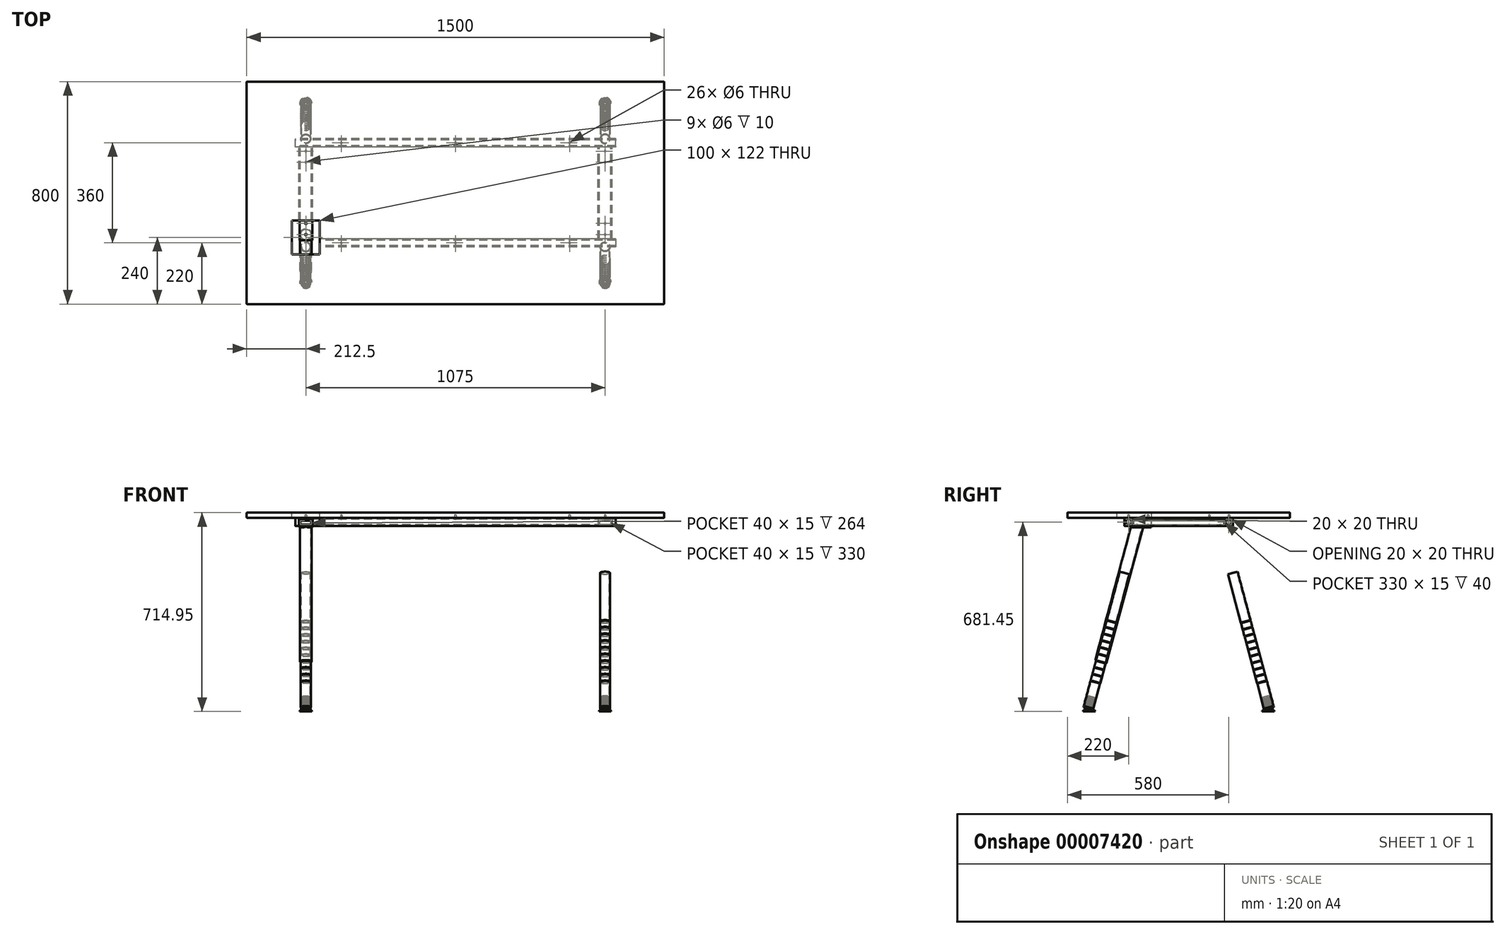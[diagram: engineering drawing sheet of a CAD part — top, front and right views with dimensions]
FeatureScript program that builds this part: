
annotation { "Feature Type Name" : "Feature", "Feature Type Description" : "" }
export const myFeature = defineFeature(function(context is Context, id is Id, definition is map)
    precondition{}
    {
        {
            var Q0;
            Q0=qCreatedBy(makeId("Top.planeOp"),FACE);
            var sketch = newSketch(context, id + "F0", { "sketchPlane" : qUnion([Q0])});
            skLineSegment(sketch, "E0.rect.bottom", {"start": v(750, -400) * mm, "end": v(-750, -400) * mm});
            skLineSegment(sketch, "E0.rect.top", {"start": v(750, 400) * mm, "end": v(-750, 400) * mm});
            skLineSegment(sketch, "E0.rect.left", {"start": v(750, -400) * mm, "end": v(750, 400) * mm});
            skLineSegment(sketch, "E0.rect.right", {"start": v(-750, -400) * mm, "end": v(-750, 400) * mm});
            skPoint(sketch, "E0.rect.middle", {"position": v(0, 0) * mm});
            skSolve(sketch);
        }
        {
            var Q0;
            Q0 = qSketchRegion(id + "F0", true);
            extrude(context, id + "F1", {"entities" : qUnion([Q0]), "depth" : 18.5 * mm});
        }
        {
            var Q0;
            Q0=makeQuery(id+"F1.opExtrude","CAP_FACE",FACE,{"disambiguationData":[OSD([sQuery(id+"F0.wireOp",EDGE,"E0.rect.bottom"),sQuery(id+"F0.wireOp",EDGE,"E0.rect.top"),sQuery(id+"F0.wireOp",EDGE,"E0.rect.left"),sQuery(id+"F0.wireOp",EDGE,"E0.rect.right")])],"isStart":false});
            var Q1;
            Q1=makeQuery(id+"F1.opExtrude","CAP_FACE",FACE,{"disambiguationData":[OSD([sQuery(id+"F0.wireOp",EDGE,"E0.rect.bottom"),sQuery(id+"F0.wireOp",EDGE,"E0.rect.top"),sQuery(id+"F0.wireOp",EDGE,"E0.rect.left"),sQuery(id+"F0.wireOp",EDGE,"E0.rect.right")])],"isStart":true});
            var Q2;
            Q2=makeQuery(id+"F1.opExtrude","SWEPT_FACE",FACE,{"disambiguationData":[OSD([sQuery(id+"F0.wireOp",EDGE,"E0.rect.top")])]});
            var Q3;
            Q3=makeQuery(id+"F1.opExtrude","SWEPT_FACE",FACE,{"disambiguationData":[OSD([sQuery(id+"F0.wireOp",EDGE,"E0.rect.bottom")])]});
            fillet(context, id + "F2", {"entities" : qUnion([Q0, Q1, Q2, Q3]), "radius" : 2 * mm, "tangentPropagation" : true, "allowEdgeOverflow" : false});
        }
        {
            var Q0;
            Q0=qCreatedBy(makeId("Top.planeOp"),FACE);
            var sketch = newSketch(context, id + "F3", { "sketchPlane" : qUnion([Q0])});
            skLineSegment(sketch, "E1.rect.bottom", {"start": v(537.5, 180) * mm, "end": v(-537.5, 180) * mm, "construction": true});
            skLineSegment(sketch, "E1.rect.top", {"start": v(537.5, -180) * mm, "end": v(-537.5, -180) * mm, "construction": true});
            skLineSegment(sketch, "E1.rect.left", {"start": v(537.5, 180) * mm, "end": v(537.5, -180) * mm, "construction": true});
            skLineSegment(sketch, "E1.rect.right", {"start": v(-537.5, 180) * mm, "end": v(-537.5, -180) * mm, "construction": true});
            skPoint(sketch, "E1.rect.middle", {"position": v(0, 0) * mm});
            skCircle(sketch, "E2", {"center": v(-410, 180) * mm, "radius": 3 * mm});
            skCircle(sketch, "E3", {"center": v(0, 180) * mm, "radius": 3 * mm});
            skCircle(sketch, "E4", {"center": v(410, 180) * mm, "radius": 3 * mm});
            skCircle(sketch, "E5", {"center": v(410, -180) * mm, "radius": 3 * mm});
            skCircle(sketch, "E6", {"center": v(0, -180) * mm, "radius": 3 * mm});
            skCircle(sketch, "E7", {"center": v(-410, -180) * mm, "radius": 3 * mm});
            skCircle(sketch, "E8", {"center": v(-537.5, 110) * mm, "radius": 3 * mm});
            skCircle(sketch, "E9", {"center": v(-537.5, -110) * mm, "radius": 3 * mm});
            skCircle(sketch, "E10", {"center": v(537.5, 110) * mm, "radius": 3 * mm});
            skCircle(sketch, "E11", {"center": v(537.5, -110) * mm, "radius": 3 * mm});
            skLineSegment(sketch, "E12", {"start": v(0, 180) * mm, "end": v(0, -180) * mm, "construction": true});
            skLineSegment(sketch, "E13", {"start": v(-537.5, 0) * mm, "end": v(537.5, 0) * mm, "construction": true});
            skCircle(sketch, "E14", {"center": v(-537.5, -150) * mm, "radius": 3 * mm, "construction": true});
            skCircle(sketch, "E15", {"center": v(537.5, -150) * mm, "radius": 3 * mm, "construction": true});
            skCircle(sketch, "E16", {"center": v(537.5, 150) * mm, "radius": 3 * mm, "construction": true});
            skCircle(sketch, "E17", {"center": v(-537.5, 150) * mm, "radius": 3 * mm, "construction": true});
            skSolve(sketch);
        }
        {
            var Q0;
            Q0 = qSketchRegion(id + "F3", true);
            extrude(context, id + "F4", {"entities" : qUnion([Q0]), "operationType" : NewBodyOperationType.REMOVE, "depth" : 10 * mm});
        }
        {
            var Q0;
            Q0=qCreatedBy(makeId("Right.planeOp"),FACE);
            var sketch = newSketch(context, id + "F5", { "sketchPlane" : qUnion([Q0])});
            skLineSegment(sketch, "E18.rect.bottom", {"start": v(-165, 0) * mm, "end": v(-195, 0) * mm});
            skLineSegment(sketch, "E18.rect.top", {"start": v(-165, -30) * mm, "end": v(-195, -30) * mm});
            skLineSegment(sketch, "E18.rect.left", {"start": v(-165, 0) * mm, "end": v(-165, -30) * mm});
            skLineSegment(sketch, "E18.rect.right", {"start": v(-195, 0) * mm, "end": v(-195, -30) * mm});
            skPoint(sketch, "E18.rect.middle", {"position": v(-180, -15) * mm});
            skLineSegment(sketch, "E19.rect.bottom", {"start": v(-170, -5) * mm, "end": v(-190, -5) * mm});
            skLineSegment(sketch, "E19.rect.top", {"start": v(-170, -25) * mm, "end": v(-190, -25) * mm});
            skLineSegment(sketch, "E19.rect.left", {"start": v(-170, -5) * mm, "end": v(-170, -25) * mm});
            skLineSegment(sketch, "E19.rect.right", {"start": v(-190, -5) * mm, "end": v(-190, -25) * mm});
            skLineSegment(sketch, "E20.rect.bottom", {"start": v(165, 0) * mm, "end": v(195, 0) * mm});
            skLineSegment(sketch, "E20.rect.top", {"start": v(165, -30) * mm, "end": v(195, -30) * mm});
            skLineSegment(sketch, "E20.rect.left", {"start": v(165, 0) * mm, "end": v(165, -30) * mm});
            skLineSegment(sketch, "E20.rect.right", {"start": v(195, 0) * mm, "end": v(195, -30) * mm});
            skPoint(sketch, "E20.rect.middle", {"position": v(180, -15) * mm});
            skLineSegment(sketch, "E21.rect.bottom", {"start": v(170, -5) * mm, "end": v(190, -5) * mm});
            skLineSegment(sketch, "E21.rect.top", {"start": v(170, -25) * mm, "end": v(190, -25) * mm});
            skLineSegment(sketch, "E21.rect.left", {"start": v(170, -5) * mm, "end": v(170, -25) * mm});
            skLineSegment(sketch, "E21.rect.right", {"start": v(190, -5) * mm, "end": v(190, -25) * mm});
            skLineSegment(sketch, "E22", {"start": v(0, -15) * mm, "end": v(0, 0) * mm, "construction": true});
            skLineSegment(sketch, "E23", {"start": v(-180, -15) * mm, "end": v(180, -15) * mm, "construction": true});
            skSolve(sketch);
        }
        {
            var Q0;
            Q0=makeQuery(id+"F5.imprint","IMPRINT",FACE,{"disambiguationData":[TD([[makeQuery(id+"F5.imprint","IMPRINT",EDGE,{"derivedFrom":sQuery(id+"F5.wireOp",EDGE,"E18.rect.bottom")}),1.0]])]});
            var Q1;
            Q1=makeQuery(id+"F5.imprint","IMPRINT",FACE,{"disambiguationData":[TD([[makeQuery(id+"F5.imprint","IMPRINT",EDGE,{"derivedFrom":sQuery(id+"F5.wireOp",EDGE,"E20.rect.bottom")}),-1.0]])]});
            extrude(context, id + "F6", {"entities" : qUnion([Q0, Q1]), "depth" : 1150 * mm, "symmetric" : true});
        }
        {
            var Q0;
            Q0=qCreatedBy(makeId("Front.planeOp"),FACE);
            var sketch = newSketch(context, id + "F7", { "sketchPlane" : qUnion([Q0])});
            skLineSegment(sketch, "E24.rect.bottom", {"start": v(-512.5, -30) * mm, "end": v(-562.5, -30) * mm});
            skLineSegment(sketch, "E24.rect.top", {"start": v(-512.5, -5) * mm, "end": v(-562.5, -5) * mm});
            skLineSegment(sketch, "E24.rect.left", {"start": v(-512.5, -30) * mm, "end": v(-512.5, -5) * mm});
            skLineSegment(sketch, "E24.rect.right", {"start": v(-562.5, -30) * mm, "end": v(-562.5, -5) * mm});
            skPoint(sketch, "E24.rect.middle", {"position": v(-537.5, -17.5) * mm});
            skLineSegment(sketch, "E25.rect.bottom", {"start": v(-517.5, -10) * mm, "end": v(-557.5, -10) * mm});
            skLineSegment(sketch, "E25.rect.top", {"start": v(-517.5, -25) * mm, "end": v(-557.5, -25) * mm});
            skLineSegment(sketch, "E25.rect.left", {"start": v(-517.5, -10) * mm, "end": v(-517.5, -25) * mm});
            skLineSegment(sketch, "E25.rect.right", {"start": v(-557.5, -10) * mm, "end": v(-557.5, -25) * mm});
            skLineSegment(sketch, "E26.rect.bottom", {"start": v(557.5, -10) * mm, "end": v(517.5, -10) * mm});
            skLineSegment(sketch, "E26.rect.top", {"start": v(557.5, -25) * mm, "end": v(517.5, -25) * mm});
            skLineSegment(sketch, "E26.rect.left", {"start": v(557.5, -10) * mm, "end": v(557.5, -25) * mm});
            skLineSegment(sketch, "E26.rect.right", {"start": v(517.5, -10) * mm, "end": v(517.5, -25) * mm});
            skPoint(sketch, "E26.rect.middle", {"position": v(537.5, -17.5) * mm});
            skLineSegment(sketch, "E27.rect.bottom", {"start": v(562.5, -5) * mm, "end": v(512.5, -5) * mm});
            skLineSegment(sketch, "E27.rect.top", {"start": v(562.5, -30) * mm, "end": v(512.5, -30) * mm});
            skLineSegment(sketch, "E27.rect.left", {"start": v(562.5, -5) * mm, "end": v(562.5, -30) * mm});
            skLineSegment(sketch, "E27.rect.right", {"start": v(512.5, -5) * mm, "end": v(512.5, -30) * mm});
            skLineSegment(sketch, "E28", {"start": v(-537.5, -17.5) * mm, "end": v(537.5, -17.5) * mm, "construction": true});
            skLineSegment(sketch, "E29", {"start": v(0, 0) * mm, "end": v(0, -17.5) * mm, "construction": true});
            skSolve(sketch);
        }
        {
            var Q0;
            Q0 = qSketchRegion(id + "F7", true);
            var Q1;
            Q1=makeQuery(id+"F6.opExtrude","SWEPT_FACE",FACE,{"disambiguationData":[OSD([sQuery(id+"F5.wireOp",EDGE,"E18.rect.left")])]});
            extrude(context, id + "F8", {"entities" : qUnion([Q0]), "endBoundEntity" : qUnion([Q1]), "depth" : 330 * mm, "symmetric" : true});
        }
        {
            var Q0;
            Q0 = qSketchRegion(id + "F3", true);
            extrude(context, id + "F9", {"entities" : qUnion([Q0]), "operationType" : NewBodyOperationType.REMOVE, "endBound" : BoundingType.THROUGH_ALL, "oppositeDirection" : true, "depth" : 25 * mm});
        }
        {
            var Q0;
            Q0=qCreatedBy(makeId("Top.planeOp"),FACE);
            var sketch = newSketch(context, id + "F10", { "sketchPlane" : qUnion([Q0])});
            skCircle(sketch, "E30.0", {"center": v(-537.5, -150) * mm, "radius": 3 * mm});
            skCircle(sketch, "E30.1", {"center": v(-537.5, 150) * mm, "radius": 3 * mm});
            skCircle(sketch, "E30.2", {"center": v(537.5, 150) * mm, "radius": 3 * mm});
            skCircle(sketch, "E30.3", {"center": v(537.5, -150) * mm, "radius": 3 * mm});
            skSolve(sketch);
        }
        {
            var Q0;
            Q0 = qSketchRegion(id + "F10", true);
            extrude(context, id + "F11", {"entities" : qUnion([Q0]), "operationType" : NewBodyOperationType.REMOVE, "endBound" : BoundingType.THROUGH_ALL, "oppositeDirection" : true, "depth" : 25 * mm});
        }
        {
            var Q0;
            Q0=makeQuery(id+"F6.opExtrude","SWEPT_BODY",BODY,{"disambiguationData":[OSD([sQuery(id+"F5.wireOp",EDGE,"E18.rect.bottom"),sQuery(id+"F5.wireOp",EDGE,"E18.rect.top"),sQuery(id+"F5.wireOp",EDGE,"E18.rect.left"),sQuery(id+"F5.wireOp",EDGE,"E18.rect.right"),sQuery(id+"F5.wireOp",EDGE,"E19.rect.bottom"),sQuery(id+"F5.wireOp",EDGE,"E19.rect.top"),sQuery(id+"F5.wireOp",EDGE,"E19.rect.left"),sQuery(id+"F5.wireOp",EDGE,"E19.rect.right")])]});
            var Q1;
            Q1=makeQuery(id+"F6.opExtrude","SWEPT_BODY",BODY,{"disambiguationData":[OSD([sQuery(id+"F5.wireOp",EDGE,"E20.rect.bottom"),sQuery(id+"F5.wireOp",EDGE,"E20.rect.top"),sQuery(id+"F5.wireOp",EDGE,"E20.rect.left"),sQuery(id+"F5.wireOp",EDGE,"E20.rect.right"),sQuery(id+"F5.wireOp",EDGE,"E21.rect.bottom"),sQuery(id+"F5.wireOp",EDGE,"E21.rect.top"),sQuery(id+"F5.wireOp",EDGE,"E21.rect.left"),sQuery(id+"F5.wireOp",EDGE,"E21.rect.right")])]});
            var Q2;
            Q2=makeQuery(id+"F8.opExtrude","SWEPT_BODY",BODY,{"disambiguationData":[OSD([sQuery(id+"F7.wireOp",EDGE,"E24.rect.bottom"),sQuery(id+"F7.wireOp",EDGE,"E24.rect.top"),sQuery(id+"F7.wireOp",EDGE,"E24.rect.left"),sQuery(id+"F7.wireOp",EDGE,"E24.rect.right"),sQuery(id+"F7.wireOp",EDGE,"E25.rect.bottom"),sQuery(id+"F7.wireOp",EDGE,"E25.rect.top"),sQuery(id+"F7.wireOp",EDGE,"E25.rect.left"),sQuery(id+"F7.wireOp",EDGE,"E25.rect.right")])]});
            var Q3;
            Q3=makeQuery(id+"F8.opExtrude","SWEPT_BODY",BODY,{"disambiguationData":[OSD([sQuery(id+"F7.wireOp",EDGE,"E26.rect.bottom"),sQuery(id+"F7.wireOp",EDGE,"E26.rect.top"),sQuery(id+"F7.wireOp",EDGE,"E26.rect.left"),sQuery(id+"F7.wireOp",EDGE,"E26.rect.right"),sQuery(id+"F7.wireOp",EDGE,"E27.rect.bottom"),sQuery(id+"F7.wireOp",EDGE,"E27.rect.top"),sQuery(id+"F7.wireOp",EDGE,"E27.rect.left"),sQuery(id+"F7.wireOp",EDGE,"E27.rect.right")])]});
            booleanBodies(context, id + "F12", {"operationType" : BooleanOperationType.UNION, "tools" : qUnion([Q0, Q1, Q2, Q3])});
        }
        {
            var Q0;
            Q0=makeQuery(id+"F6.opExtrude","SWEPT_EDGE",EDGE,{"disambiguationData":[OSD([sQuery(id+"F5.wireOp",EDGE,"E20.rect.bottom"),sQuery(id+"F5.wireOp",EDGE,"E20.rect.left")])]});
            var Q1;
            Q1=makeQuery(id+"F6.opExtrude","SWEPT_EDGE",EDGE,{"disambiguationData":[OSD([sQuery(id+"F5.wireOp",EDGE,"E20.rect.top"),sQuery(id+"F5.wireOp",EDGE,"E20.rect.left")])]});
            var Q2;
            Q2=makeQuery(id+"F6.opExtrude","SWEPT_EDGE",EDGE,{"disambiguationData":[OSD([sQuery(id+"F5.wireOp",EDGE,"E20.rect.top"),sQuery(id+"F5.wireOp",EDGE,"E20.rect.right")])]});
            var Q3;
            Q3=makeQuery(id+"F6.opExtrude","SWEPT_EDGE",EDGE,{"disambiguationData":[OSD([sQuery(id+"F5.wireOp",EDGE,"E20.rect.bottom"),sQuery(id+"F5.wireOp",EDGE,"E20.rect.right")])]});
            var Q4;
            Q4=makeQuery(id+"F6.opExtrude","SWEPT_EDGE",EDGE,{"disambiguationData":[OSD([sQuery(id+"F5.wireOp",EDGE,"E18.rect.top"),sQuery(id+"F5.wireOp",EDGE,"E18.rect.left")])]});
            var Q5;
            Q5=makeQuery(id+"F6.opExtrude","SWEPT_EDGE",EDGE,{"disambiguationData":[OSD([sQuery(id+"F5.wireOp",EDGE,"E18.rect.bottom"),sQuery(id+"F5.wireOp",EDGE,"E18.rect.left")])]});
            var Q6;
            Q6=makeQuery(id+"F6.opExtrude","SWEPT_EDGE",EDGE,{"disambiguationData":[OSD([sQuery(id+"F5.wireOp",EDGE,"E18.rect.top"),sQuery(id+"F5.wireOp",EDGE,"E18.rect.right")])]});
            var Q7;
            Q7=makeQuery(id+"F6.opExtrude","SWEPT_EDGE",EDGE,{"disambiguationData":[OSD([sQuery(id+"F5.wireOp",EDGE,"E18.rect.bottom"),sQuery(id+"F5.wireOp",EDGE,"E18.rect.right")])]});
            var Q8;
            Q8=makeQuery(id+"F6.opExtrude","SWEPT_EDGE",EDGE,{"disambiguationData":[OSD([sQuery(id+"F5.wireOp",EDGE,"E21.rect.bottom"),sQuery(id+"F5.wireOp",EDGE,"E21.rect.right")])]});
            var Q9;
            Q9=makeQuery(id+"F8.opExtrude","SWEPT_EDGE",EDGE,{"disambiguationData":[OSD([sQuery(id+"F7.wireOp",EDGE,"E24.rect.top"),sQuery(id+"F7.wireOp",EDGE,"E24.rect.right")])]});
            var Q10;
            Q10=makeQuery(id+"F8.opExtrude","SWEPT_EDGE",EDGE,{"disambiguationData":[OSD([sQuery(id+"F7.wireOp",EDGE,"E24.rect.bottom"),sQuery(id+"F7.wireOp",EDGE,"E24.rect.right")])]});
            var Q11;
            Q11=makeQuery(id+"F8.opExtrude","SWEPT_EDGE",EDGE,{"disambiguationData":[OSD([sQuery(id+"F7.wireOp",EDGE,"E24.rect.bottom"),sQuery(id+"F7.wireOp",EDGE,"E24.rect.left")])]});
            var Q12;
            Q12=makeQuery(id+"F8.opExtrude","SWEPT_EDGE",EDGE,{"disambiguationData":[OSD([sQuery(id+"F7.wireOp",EDGE,"E24.rect.top"),sQuery(id+"F7.wireOp",EDGE,"E24.rect.left")])]});
            var Q13;
            Q13=makeQuery(id+"F8.opExtrude","SWEPT_EDGE",EDGE,{"disambiguationData":[OSD([sQuery(id+"F7.wireOp",EDGE,"E27.rect.bottom"),sQuery(id+"F7.wireOp",EDGE,"E27.rect.right")])]});
            var Q14;
            Q14=makeQuery(id+"F8.opExtrude","SWEPT_EDGE",EDGE,{"disambiguationData":[OSD([sQuery(id+"F7.wireOp",EDGE,"E27.rect.top"),sQuery(id+"F7.wireOp",EDGE,"E27.rect.right")])]});
            var Q15;
            Q15=makeQuery(id+"F8.opExtrude","SWEPT_EDGE",EDGE,{"disambiguationData":[OSD([sQuery(id+"F7.wireOp",EDGE,"E27.rect.top"),sQuery(id+"F7.wireOp",EDGE,"E27.rect.left")])]});
            var Q16;
            Q16=makeQuery(id+"F8.opExtrude","SWEPT_EDGE",EDGE,{"disambiguationData":[OSD([sQuery(id+"F7.wireOp",EDGE,"E27.rect.bottom"),sQuery(id+"F7.wireOp",EDGE,"E27.rect.left")])]});
            fillet(context, id + "F13", {"entities" : qUnion([Q0, Q1, Q2, Q3, Q4, Q5, Q6, Q7, Q8, Q9, Q10, Q11, Q12, Q13, Q14, Q15, Q16]), "radius" : 2 * mm, "tangentPropagation" : true, "allowEdgeOverflow" : false});
        }
        {
            var Q0;
            Q0=makeQuery(id+"F12.opBoolean","MERGE",FACE,{"derivedFrom":[makeQuery(id+"F6.opExtrude","SWEPT_FACE",FACE,{"disambiguationData":[OSD([sQuery(id+"F5.wireOp",EDGE,"E18.rect.top")])]}),makeQuery(id+"F6.opExtrude","SWEPT_FACE",FACE,{"disambiguationData":[OSD([sQuery(id+"F5.wireOp",EDGE,"E20.rect.top")])]}),makeQuery(id+"F8.opExtrude","SWEPT_FACE",FACE,{"disambiguationData":[OSD([sQuery(id+"F7.wireOp",EDGE,"E24.rect.bottom")])]}),makeQuery(id+"F8.opExtrude","SWEPT_FACE",FACE,{"disambiguationData":[OSD([sQuery(id+"F7.wireOp",EDGE,"E27.rect.top")])]})]});
            var sketch = newSketch(context, id + "F14", { "sketchPlane" : qUnion([Q0])});
            skLineSegment(sketch, "E31.bottom", {"start": v(-560.5, 99) * mm, "end": v(-514.5, 99) * mm});
            skLineSegment(sketch, "E31.top", {"start": v(-560.5, 171) * mm, "end": v(-514.5, 171) * mm});
            skLineSegment(sketch, "E31.left", {"start": v(-560.5, 99) * mm, "end": v(-560.5, 171) * mm});
            skLineSegment(sketch, "E31.right", {"start": v(-514.5, 99) * mm, "end": v(-514.5, 171) * mm});
            skLineSegment(sketch, "E32", {"start": v(-537.5, 110) * mm, "end": v(-537.5, 99) * mm, "construction": true});
            skLineSegment(sketch, "E33", {"start": v(-537.5, 150) * mm, "end": v(-537.5, 171) * mm, "construction": true});
            skCircle(sketch, "E34.0", {"center": v(-537.5, 150) * mm, "radius": 3 * mm});
            skCircle(sketch, "E34.1", {"center": v(-537.5, 110) * mm, "radius": 3 * mm});
            skSolve(sketch);
        }
        {
            var Q0;
            Q0 = qSketchRegion(id + "F14", true);
            extrude(context, id + "F15", {"entities" : qUnion([Q0]), "depth" : 4 * mm});
        }
        {
            var Q0;
            Q0=makeQuery(id+"F15.opExtrude","SWEPT_FACE",FACE,{"disambiguationData":[OSD([sQuery(id+"F14.wireOp",EDGE,"E31.left")])]});
            var Q1;
            Q1=makeQuery(id+"F15.opExtrude","SWEPT_FACE",FACE,{"disambiguationData":[OSD([sQuery(id+"F14.wireOp",EDGE,"E31.right")])]});
            cPlane(context, id + "F16", {"entities" : qUnion([Q0, Q1]), "cplaneType" : CPlaneType.MID_PLANE, "offset" : 150 * mm, "width" : 150 * mm, "height" : 150 * mm});
        }
        {
            var Q0;
            Q0=qCreatedBy(id+"F16.planeOp",FACE);
            var sketch = newSketch(context, id + "F17", { "sketchPlane" : qUnion([Q0])});
            skLineSegment(sketch, "E35.0", {"start": v(153, -34) * mm, "end": v(147, -34) * mm});
            skLineSegment(sketch, "E36", {"start": v(150, -34) * mm, "end": v(279.4, -516.96) * mm, "construction": true});
            skLineSegment(sketch, "E37", {"start": v(194.09, -198.54) * mm, "end": v(323.5, -681.5) * mm, "construction": true});
            skLineSegment(sketch, "E38", {"start": v(297.28, -512.17) * mm, "end": v(167.87, -29.21) * mm});
            skLineSegment(sketch, "E39", {"start": v(167.87, -29.21) * mm, "end": v(170.28, -28.56) * mm, "construction": true});
            skLineSegment(sketch, "E40", {"start": v(170.28, -28.56) * mm, "end": v(299.7, -511.53) * mm});
            skLineSegment(sketch, "E41", {"start": v(299.7, -511.53) * mm, "end": v(297.28, -512.17) * mm});
            skLineSegment(sketch, "E42", {"start": v(150, -34) * mm, "end": v(167.87, -29.21) * mm});
            skLineSegment(sketch, "E43", {"start": v(167.87, -29.21) * mm, "end": v(163.99, -14.72) * mm});
            skLineSegment(sketch, "E44", {"start": v(163.99, -14.72) * mm, "end": v(166.4, -14.08) * mm});
            skLineSegment(sketch, "E45", {"start": v(166.4, -14.08) * mm, "end": v(170.28, -28.56) * mm});
            skLineSegment(sketch, "E46", {"start": v(209.06, -194.53) * mm, "end": v(338.47, -677.49) * mm});
            skLineSegment(sketch, "E47", {"start": v(338.47, -677.49) * mm, "end": v(340.88, -676.84) * mm});
            skLineSegment(sketch, "E48", {"start": v(340.88, -676.84) * mm, "end": v(316.81, -587.01) * mm});
            skLineSegment(sketch, "E49", {"start": v(211.47, -193.88) * mm, "end": v(209.06, -194.53) * mm});
            skLineSegment(sketch, "E50", {"start": v(209.06, -194.53) * mm, "end": v(194.09, -198.54) * mm});
            skArc(sketch, "E51", {"start": v(316.3, -585.08) * mm, "mid": v(315.59, -586.3) * mm, "end": v(316.81, -587.01) * mm});
            skLineSegment(sketch, "E52.trimOffspring", {"start": v(316.3, -585.08) * mm, "end": v(211.47, -193.88) * mm});
            skArc(sketch, "E53.1.0.0", {"start": v(309.83, -560.93) * mm, "mid": v(309.12, -562.15) * mm, "end": v(310.34, -562.86) * mm});
            skArc(sketch, "E53.2.0.0", {"start": v(303.36, -536.78) * mm, "mid": v(302.65, -538) * mm, "end": v(303.87, -538.71) * mm});
            skLineSegment(sketch, "E53.direction1", {"start": v(316.81, -587.01) * mm, "end": v(310.34, -562.86) * mm, "construction": true});
            skArc(sketch, "E54.0.3.0", {"start": v(296.88, -512.63) * mm, "mid": v(296.18, -513.86) * mm, "end": v(297.4, -514.57) * mm});
            skArc(sketch, "E54.0.4.0", {"start": v(290.41, -488.49) * mm, "mid": v(289.7, -489.71) * mm, "end": v(290.93, -490.42) * mm});
            skArc(sketch, "E54.0.5.0", {"start": v(283.94, -464.34) * mm, "mid": v(283.24, -465.56) * mm, "end": v(284.46, -466.27) * mm});
            skArc(sketch, "E54.0.6.0", {"start": v(277.47, -440.19) * mm, "mid": v(276.77, -441.41) * mm, "end": v(278, -442.12) * mm});
            skArc(sketch, "E54.0.7.0", {"start": v(271, -416.04) * mm, "mid": v(270.3, -417.27) * mm, "end": v(271.52, -417.97) * mm});
            skArc(sketch, "E54.0.8.0", {"start": v(264.53, -391.9) * mm, "mid": v(263.83, -393.12) * mm, "end": v(265.05, -393.82) * mm});
            skArc(sketch, "E54.0.9.0", {"start": v(258.06, -367.74) * mm, "mid": v(257.35, -368.97) * mm, "end": v(258.58, -369.68) * mm});
            skLineSegment(sketch, "E55.0.0", {"start": v(398, 18.5) * mm, "end": v(-398, 18.5) * mm, "construction": true});
            skLineSegment(sketch, "E55.0.2", {"start": v(-398, 18.5) * mm, "end": v(398, 18.5) * mm});
            skSolve(sketch);
        }
        {
            var Q0;
            Q0=makeQuery(id+"F17.imprint","IMPRINT",FACE,{"disambiguationData":[TD([[makeQuery(id+"F17.imprint","IMPRINT",EDGE,{"derivedFrom":sQuery(id+"F17.wireOp",EDGE,"E38")}),-1.0]])]});
            var Q1;
            Q1=sQuery(id+"F17.wireOp",EDGE,"E36");
            revolve(context, id + "F18", {"operationType" : NewBodyOperationType.ADD, "entities" : qUnion([Q0]), "axis" : qUnion([Q1]), "revolveType" : RevolveType.FULL});
        }
        {
            var Q0;
            Q0=qCreatedBy(id+"F16.planeOp",FACE);
            var sketch = newSketch(context, id + "F19", { "sketchPlane" : qUnion([Q0])});
            skLineSegment(sketch, "E56.0", {"start": v(171, -30) * mm, "end": v(99, -30) * mm});
            skLineSegment(sketch, "E57", {"start": v(171, -30) * mm, "end": v(221, -30) * mm});
            skLineSegment(sketch, "E58", {"start": v(221, -30) * mm, "end": v(221, 40) * mm});
            skLineSegment(sketch, "E59", {"start": v(221, 40) * mm, "end": v(99, 40) * mm});
            skLineSegment(sketch, "E60", {"start": v(99, 40) * mm, "end": v(99, -30) * mm});
            skSolve(sketch);
        }
        {
            var Q0;
            Q0=makeQuery(id+"F19.imprint","IMPRINT",FACE,{"disambiguationData":[TD([[makeQuery(id+"F19.imprint","IMPRINT",EDGE,{"derivedFrom":sQuery(id+"F19.wireOp",EDGE,"E56.0")}),-1.0]])]});
            extrude(context, id + "F20", {"entities" : qUnion([Q0]), "operationType" : NewBodyOperationType.REMOVE, "oppositeDirection" : true, "depth" : 100 * mm, "symmetric" : true});
        }
        {
            var Q0;
            Q0=makeQuery(id+"F17.imprint","IMPRINT",FACE,{"disambiguationData":[TD([[makeQuery(id+"F17.imprint","IMPRINT",EDGE,{"derivedFrom":sQuery(id+"F17.wireOp",EDGE,"E46")}),1.0]])]});
            var Q1;
            Q1=sQuery(id+"F17.wireOp",EDGE,"E37");
            revolve(context, id + "F21", {"entities" : qUnion([Q0]), "axis" : qUnion([Q1]), "revolveType" : RevolveType.FULL});
        }
        {
            var Q0;
            Q0=qCreatedBy(id+"F16.planeOp",FACE);
            var sketch = newSketch(context, id + "F22", { "sketchPlane" : qUnion([Q0])});
            skLineSegment(sketch, "E61", {"start": v(329.32, -643.7) * mm, "end": v(330.44, -647.17) * mm});
            skLineSegment(sketch, "E62", {"start": v(341.7, -681.8) * mm, "end": v(340.73, -682.06) * mm});
            skLineSegment(sketch, "E63", {"start": v(334.6, -678.52) * mm, "end": v(324.25, -639.89) * mm});
            skLineSegment(sketch, "E64", {"start": v(324.25, -639.89) * mm, "end": v(329.32, -643.7) * mm});
            skLineSegment(sketch, "E65", {"start": v(330.44, -647.17) * mm, "end": v(331.57, -650.63) * mm});
            skLineSegment(sketch, "E66", {"start": v(331.57, -650.63) * mm, "end": v(332.7, -654.1) * mm});
            skLineSegment(sketch, "E67", {"start": v(332.7, -654.1) * mm, "end": v(333.82, -657.56) * mm});
            skLineSegment(sketch, "E68", {"start": v(333.82, -657.56) * mm, "end": v(334.94, -661.02) * mm});
            skLineSegment(sketch, "E69", {"start": v(334.94, -661.02) * mm, "end": v(336.07, -664.48) * mm});
            skLineSegment(sketch, "E70", {"start": v(336.07, -664.48) * mm, "end": v(337.2, -667.95) * mm});
            skLineSegment(sketch, "E71", {"start": v(337.2, -667.95) * mm, "end": v(338.32, -671.41) * mm});
            skLineSegment(sketch, "E72", {"start": v(338.32, -671.41) * mm, "end": v(339.44, -674.87) * mm});
            skLineSegment(sketch, "E73", {"start": v(339.44, -674.87) * mm, "end": v(340.57, -678.34) * mm});
            skLineSegment(sketch, "E74", {"start": v(340.57, -678.34) * mm, "end": v(341.7, -681.8) * mm});
            skLineSegment(sketch, "E75", {"start": v(340.57, -678.34) * mm, "end": v(338, -676.92) * mm});
            skLineSegment(sketch, "E76", {"start": v(338, -676.92) * mm, "end": v(339.44, -674.87) * mm});
            skLineSegment(sketch, "E77", {"start": v(339.44, -674.87) * mm, "end": v(336.88, -673.46) * mm});
            skLineSegment(sketch, "E78", {"start": v(336.88, -673.46) * mm, "end": v(338.32, -671.41) * mm});
            skLineSegment(sketch, "E79", {"start": v(338.32, -671.41) * mm, "end": v(335.76, -670) * mm});
            skLineSegment(sketch, "E80", {"start": v(335.76, -670) * mm, "end": v(337.2, -667.95) * mm});
            skLineSegment(sketch, "E81", {"start": v(337.2, -667.95) * mm, "end": v(334.63, -666.53) * mm});
            skLineSegment(sketch, "E82", {"start": v(334.63, -666.53) * mm, "end": v(336.07, -664.48) * mm});
            skLineSegment(sketch, "E83", {"start": v(336.07, -664.48) * mm, "end": v(333.5, -663.07) * mm});
            skLineSegment(sketch, "E84", {"start": v(333.5, -663.07) * mm, "end": v(334.94, -661.02) * mm});
            skLineSegment(sketch, "E85", {"start": v(334.94, -661.02) * mm, "end": v(332.38, -659.6) * mm});
            skLineSegment(sketch, "E86", {"start": v(332.38, -659.6) * mm, "end": v(333.82, -657.56) * mm});
            skLineSegment(sketch, "E87", {"start": v(333.82, -657.56) * mm, "end": v(331.25, -656.14) * mm});
            skLineSegment(sketch, "E88", {"start": v(331.25, -656.14) * mm, "end": v(332.7, -654.1) * mm});
            skLineSegment(sketch, "E89", {"start": v(332.7, -654.1) * mm, "end": v(330.13, -652.68) * mm});
            skLineSegment(sketch, "E90", {"start": v(330.13, -652.68) * mm, "end": v(331.57, -650.63) * mm});
            skLineSegment(sketch, "E91", {"start": v(331.57, -650.63) * mm, "end": v(329, -649.21) * mm});
            skLineSegment(sketch, "E92", {"start": v(329, -649.21) * mm, "end": v(330.44, -647.17) * mm});
            skLineSegment(sketch, "E93", {"start": v(330.44, -647.17) * mm, "end": v(327.88, -645.75) * mm});
            skLineSegment(sketch, "E94", {"start": v(327.88, -645.75) * mm, "end": v(329.32, -643.7) * mm});
            skLineSegment(sketch, "E95", {"start": v(329.32, -643.7) * mm, "end": v(325.55, -644.72) * mm, "construction": true});
            skLineSegment(sketch, "E96.0", {"start": v(338.47, -677.49) * mm, "end": v(340.88, -676.84) * mm, "construction": true});
            skLineSegment(sketch, "E96.1", {"start": v(209.06, -194.53) * mm, "end": v(338.47, -677.49) * mm, "construction": true});
            skLineSegment(sketch, "E96.2", {"start": v(194.09, -198.54) * mm, "end": v(323.5, -681.5) * mm, "construction": true});
            skLineSegment(sketch, "E96.3", {"start": v(340.88, -676.84) * mm, "end": v(316.81, -587.01) * mm, "construction": true});
            skArc(sketch, "E97", {"start": v(334.6, -678.52) * mm, "mid": v(334.7, -671.18) * mm, "end": v(330.94, -664.86) * mm});
            skPoint(sketch, "E98.visualSharp", {"position": v(335.9, -683.35) * mm});
            skArc(sketch, "E98.filletArc", {"start": v(334.6, -678.52) * mm, "mid": v(336.93, -681.56) * mm, "end": v(340.73, -682.06) * mm});
            skSolve(sketch);
        }
        {
            var Q0;
            Q0=makeQuery(id+"F22.imprint","IMPRINT",FACE,{"disambiguationData":[TD([[makeQuery(id+"F22.imprint","IMPRINT",EDGE,{"derivedFrom":sQuery(id+"F22.wireOp",EDGE,"E62")}),-1.0]])]});
            var Q1;
            Q1=sQuery(id+"F22.wireOp",EDGE,"E96.2");
            revolve(context, id + "F23", {"entities" : qUnion([Q0]), "axis" : qUnion([Q1]), "revolveType" : RevolveType.FULL});
        }
        {
            var Q0;
            Q0=makeQuery(id+"F23.opRevolve","SWEPT_EDGE",EDGE,{"disambiguationData":[OSD([sQuery(id+"F22.wireOp",EDGE,"E68"),sQuery(id+"F22.wireOp",EDGE,"E69"),sQuery(id+"F22.wireOp",EDGE,"E84"),sQuery(id+"F22.wireOp",EDGE,"E85")])]});
            var Q1;
            Q1=makeQuery(id+"F23.opRevolve","SWEPT_EDGE",EDGE,{"disambiguationData":[OSD([sQuery(id+"F22.wireOp",EDGE,"E69"),sQuery(id+"F22.wireOp",EDGE,"E70"),sQuery(id+"F22.wireOp",EDGE,"E82"),sQuery(id+"F22.wireOp",EDGE,"E83")])]});
            var Q2;
            Q2=makeQuery(id+"F23.opRevolve","SWEPT_EDGE",EDGE,{"disambiguationData":[OSD([sQuery(id+"F22.wireOp",EDGE,"E70"),sQuery(id+"F22.wireOp",EDGE,"E71"),sQuery(id+"F22.wireOp",EDGE,"E80"),sQuery(id+"F22.wireOp",EDGE,"E81")])]});
            var Q3;
            Q3=makeQuery(id+"F23.opRevolve","SWEPT_EDGE",EDGE,{"disambiguationData":[OSD([sQuery(id+"F22.wireOp",EDGE,"E71"),sQuery(id+"F22.wireOp",EDGE,"E72"),sQuery(id+"F22.wireOp",EDGE,"E78"),sQuery(id+"F22.wireOp",EDGE,"E79")])]});
            var Q4;
            Q4=makeQuery(id+"F23.opRevolve","SWEPT_EDGE",EDGE,{"disambiguationData":[OSD([sQuery(id+"F22.wireOp",EDGE,"E72"),sQuery(id+"F22.wireOp",EDGE,"E73"),sQuery(id+"F22.wireOp",EDGE,"E76"),sQuery(id+"F22.wireOp",EDGE,"E77")])]});
            var Q5;
            Q5=makeQuery(id+"F23.opRevolve","SWEPT_EDGE",EDGE,{"disambiguationData":[OSD([sQuery(id+"F22.wireOp",EDGE,"E73"),sQuery(id+"F22.wireOp",EDGE,"E74"),sQuery(id+"F22.wireOp",EDGE,"E75")])]});
            var Q6;
            Q6=makeQuery(id+"F23.opRevolve","SWEPT_EDGE",EDGE,{"disambiguationData":[OSD([sQuery(id+"F22.wireOp",EDGE,"E67"),sQuery(id+"F22.wireOp",EDGE,"E68"),sQuery(id+"F22.wireOp",EDGE,"E86"),sQuery(id+"F22.wireOp",EDGE,"E87")])]});
            var Q7;
            Q7=makeQuery(id+"F23.opRevolve","SWEPT_EDGE",EDGE,{"disambiguationData":[OSD([sQuery(id+"F22.wireOp",EDGE,"E66"),sQuery(id+"F22.wireOp",EDGE,"E67"),sQuery(id+"F22.wireOp",EDGE,"E88"),sQuery(id+"F22.wireOp",EDGE,"E89")])]});
            var Q8;
            Q8=makeQuery(id+"F23.opRevolve","SWEPT_EDGE",EDGE,{"disambiguationData":[OSD([sQuery(id+"F22.wireOp",EDGE,"E65"),sQuery(id+"F22.wireOp",EDGE,"E66"),sQuery(id+"F22.wireOp",EDGE,"E90"),sQuery(id+"F22.wireOp",EDGE,"E91")])]});
            var Q9;
            Q9=makeQuery(id+"F23.opRevolve","SWEPT_EDGE",EDGE,{"disambiguationData":[OSD([sQuery(id+"F22.wireOp",EDGE,"E61"),sQuery(id+"F22.wireOp",EDGE,"E65"),sQuery(id+"F22.wireOp",EDGE,"E92"),sQuery(id+"F22.wireOp",EDGE,"E93")])]});
            var Q10;
            Q10=makeQuery(id+"F23.opRevolve","SWEPT_EDGE",EDGE,{"disambiguationData":[OSD([sQuery(id+"F22.wireOp",EDGE,"E61"),sQuery(id+"F22.wireOp",EDGE,"E64"),sQuery(id+"F22.wireOp",EDGE,"E94")])]});
            chamfer(context, id + "F24", {"entities" : qUnion([Q0, Q1, Q2, Q3, Q4, Q5, Q6, Q7, Q8, Q9, Q10]), "width" : .5 * mm, "tangentPropagation" : true});
        }
        {
            var Q0;
            Q0=qCreatedBy(id+"F16.planeOp",FACE);
            var sketch = newSketch(context, id + "F25", { "sketchPlane" : qUnion([Q0])});
            skArc(sketch, "E99.0", {"start": v(334.6, -678.52) * mm, "mid": v(334.7, -671.18) * mm, "end": v(330.94, -664.86) * mm, "construction": true});
            skLineSegment(sketch, "E99.1", {"start": v(194.09, -198.54) * mm, "end": v(323.5, -681.5) * mm, "construction": true});
            skArc(sketch, "E100", {"start": v(326.67, -686.45) * mm, "mid": v(334.21, -672.12) * mm, "end": v(321.67, -661.87) * mm});
            skLineSegment(sketch, "E101", {"start": v(321.67, -661.87) * mm, "end": v(321.67, -687.47) * mm});
            skLineSegment(sketch, "E102", {"start": v(321.67, -687.47) * mm, "end": v(321.67, -696.45) * mm});
            skLineSegment(sketch, "E103", {"start": v(321.67, -696.45) * mm, "end": v(343.67, -696.45) * mm});
            skLineSegment(sketch, "E104", {"start": v(343.67, -696.45) * mm, "end": v(343.67, -696.45) * mm});
            skLineSegment(sketch, "E105", {"start": v(338.67, -691.45) * mm, "end": v(326.67, -691.45) * mm});
            skLineSegment(sketch, "E106", {"start": v(326.67, -691.45) * mm, "end": v(326.67, -686.45) * mm});
            skPoint(sketch, "E107.visualSharp", {"position": v(343.67, -691.45) * mm});
            skArc(sketch, "E107.filletArc", {"start": v(343.67, -696.45) * mm, "mid": v(342.2, -692.92) * mm, "end": v(338.67, -691.45) * mm});
            skLineSegment(sketch, "E108.0.MirrorCS", {"start": v(304.67, -691.45) * mm, "end": v(316.67, -691.45) * mm, "construction": true});
            skArc(sketch, "E108.1.MirrorCS", {"start": v(299.67, -696.45) * mm, "mid": v(301.13, -692.92) * mm, "end": v(304.67, -691.45) * mm, "construction": true});
            skSolve(sketch);
        }
        {
            var Q0;
            Q0=makeQuery(id+"F25.imprint","IMPRINT",FACE,{"disambiguationData":[TD([[makeQuery(id+"F25.imprint","IMPRINT",EDGE,{"derivedFrom":sQuery(id+"F25.wireOp",EDGE,"e8593e3d-3b37-4ffa-81d3-c2e88ce00178")}),1.0]])]});
            var Q1;
            Q1=makeQuery(id+"F25.imprint","IMPRINT",FACE,{"disambiguationData":[TD([[makeQuery(id+"F25.imprint","IMPRINT",EDGE,{"derivedFrom":sQuery(id+"F25.wireOp",EDGE,"E100")}),1.0]])]});
            var Q2;
            Q2=sQuery(id+"F25.wireOp",EDGE,"E101");
            revolve(context, id + "F26", {"entities" : qUnion([Q0, Q1]), "axis" : qUnion([Q2]), "revolveType" : RevolveType.FULL});
        }
        {
            var Q0;
            Q0=makeQuery(id+"F15.opExtrude","SWEPT_BODY",BODY,{"disambiguationData":[OSD([sQuery(id+"F14.wireOp",EDGE,"E31.bottom"),sQuery(id+"F14.wireOp",EDGE,"E31.top"),sQuery(id+"F14.wireOp",EDGE,"E31.left"),sQuery(id+"F14.wireOp",EDGE,"E31.right"),sQuery(id+"F14.wireOp",EDGE,"E34.0"),sQuery(id+"F14.wireOp",EDGE,"E34.1")])]});
            var Q1;
            Q1=makeQuery(id+"F21.opRevolve","SWEPT_BODY",BODY,{"disambiguationData":[OSD([sQuery(id+"F17.wireOp",EDGE,"E46"),sQuery(id+"F17.wireOp",EDGE,"E47"),sQuery(id+"F17.wireOp",EDGE,"E48"),sQuery(id+"F17.wireOp",EDGE,"E49"),sQuery(id+"F17.wireOp",EDGE,"E51"),sQuery(id+"F17.wireOp",EDGE,"E52.trimOffspring"),sQuery(id+"F17.wireOp",EDGE,"E53.1.0.0"),sQuery(id+"F17.wireOp",EDGE,"E53.2.0.0"),sQuery(id+"F17.wireOp",EDGE,"E54.0.3.0"),sQuery(id+"F17.wireOp",EDGE,"E54.0.4.0"),sQuery(id+"F17.wireOp",EDGE,"E54.0.5.0"),sQuery(id+"F17.wireOp",EDGE,"E54.0.6.0"),sQuery(id+"F17.wireOp",EDGE,"E54.0.7.0"),sQuery(id+"F17.wireOp",EDGE,"E54.0.8.0"),sQuery(id+"F17.wireOp",EDGE,"E54.0.9.0")])]});
            var Q2;
            Q2=makeQuery(id+"F23.opRevolve","SWEPT_BODY",BODY,{"disambiguationData":[OSD([sQuery(id+"F22.wireOp",EDGE,"E62"),sQuery(id+"F22.wireOp",EDGE,"E63"),sQuery(id+"F22.wireOp",EDGE,"E64"),sQuery(id+"F22.wireOp",EDGE,"E74"),sQuery(id+"F22.wireOp",EDGE,"E75"),sQuery(id+"F22.wireOp",EDGE,"E76"),sQuery(id+"F22.wireOp",EDGE,"E77"),sQuery(id+"F22.wireOp",EDGE,"E78"),sQuery(id+"F22.wireOp",EDGE,"E79"),sQuery(id+"F22.wireOp",EDGE,"E80"),sQuery(id+"F22.wireOp",EDGE,"E81"),sQuery(id+"F22.wireOp",EDGE,"E82"),sQuery(id+"F22.wireOp",EDGE,"E83"),sQuery(id+"F22.wireOp",EDGE,"E84"),sQuery(id+"F22.wireOp",EDGE,"E85"),sQuery(id+"F22.wireOp",EDGE,"E86"),sQuery(id+"F22.wireOp",EDGE,"E87"),sQuery(id+"F22.wireOp",EDGE,"E88"),sQuery(id+"F22.wireOp",EDGE,"E89"),sQuery(id+"F22.wireOp",EDGE,"E90"),sQuery(id+"F22.wireOp",EDGE,"E91"),sQuery(id+"F22.wireOp",EDGE,"E92"),sQuery(id+"F22.wireOp",EDGE,"E93"),sQuery(id+"F22.wireOp",EDGE,"E94"),sQuery(id+"F22.wireOp",EDGE,"E97"),sQuery(id+"F22.wireOp",EDGE,"E98.filletArc")])]});
            var Q3;
            Q3=makeQuery(id+"F26.opRevolve","SWEPT_BODY",BODY,{"disambiguationData":[OSD([sQuery(id+"F25.wireOp",EDGE,"E100"),sQuery(id+"F25.wireOp",EDGE,"E101"),sQuery(id+"F25.wireOp",EDGE,"E102"),sQuery(id+"F25.wireOp",EDGE,"E103"),sQuery(id+"F25.wireOp",EDGE,"E105"),sQuery(id+"F25.wireOp",EDGE,"E106"),sQuery(id+"F25.wireOp",EDGE,"E107.filletArc")])]});
            var Q4;
            Q4=qCreatedBy(makeId("Right.planeOp"),FACE);
            mirror(context, id + "F27", {"entities" : qUnion([Q0, Q1, Q2, Q3]), "mirrorPlane" : qUnion([Q4])});
        }
        {
            var Q0;
            Q0=makeQuery(id+"F21.opRevolve","SWEPT_BODY",BODY,{"disambiguationData":[OSD([sQuery(id+"F17.wireOp",EDGE,"E46"),sQuery(id+"F17.wireOp",EDGE,"E47"),sQuery(id+"F17.wireOp",EDGE,"E48"),sQuery(id+"F17.wireOp",EDGE,"E49"),sQuery(id+"F17.wireOp",EDGE,"E51"),sQuery(id+"F17.wireOp",EDGE,"E52.trimOffspring"),sQuery(id+"F17.wireOp",EDGE,"E53.1.0.0"),sQuery(id+"F17.wireOp",EDGE,"E53.2.0.0"),sQuery(id+"F17.wireOp",EDGE,"E54.0.3.0"),sQuery(id+"F17.wireOp",EDGE,"E54.0.4.0"),sQuery(id+"F17.wireOp",EDGE,"E54.0.5.0"),sQuery(id+"F17.wireOp",EDGE,"E54.0.6.0"),sQuery(id+"F17.wireOp",EDGE,"E54.0.7.0"),sQuery(id+"F17.wireOp",EDGE,"E54.0.8.0"),sQuery(id+"F17.wireOp",EDGE,"E54.0.9.0")])]});
            var Q1;
            Q1=makeQuery(id+"F23.opRevolve","SWEPT_BODY",BODY,{"disambiguationData":[OSD([sQuery(id+"F22.wireOp",EDGE,"E62"),sQuery(id+"F22.wireOp",EDGE,"E63"),sQuery(id+"F22.wireOp",EDGE,"E64"),sQuery(id+"F22.wireOp",EDGE,"E74"),sQuery(id+"F22.wireOp",EDGE,"E75"),sQuery(id+"F22.wireOp",EDGE,"E76"),sQuery(id+"F22.wireOp",EDGE,"E77"),sQuery(id+"F22.wireOp",EDGE,"E78"),sQuery(id+"F22.wireOp",EDGE,"E79"),sQuery(id+"F22.wireOp",EDGE,"E80"),sQuery(id+"F22.wireOp",EDGE,"E81"),sQuery(id+"F22.wireOp",EDGE,"E82"),sQuery(id+"F22.wireOp",EDGE,"E83"),sQuery(id+"F22.wireOp",EDGE,"E84"),sQuery(id+"F22.wireOp",EDGE,"E85"),sQuery(id+"F22.wireOp",EDGE,"E86"),sQuery(id+"F22.wireOp",EDGE,"E87"),sQuery(id+"F22.wireOp",EDGE,"E88"),sQuery(id+"F22.wireOp",EDGE,"E89"),sQuery(id+"F22.wireOp",EDGE,"E90"),sQuery(id+"F22.wireOp",EDGE,"E91"),sQuery(id+"F22.wireOp",EDGE,"E92"),sQuery(id+"F22.wireOp",EDGE,"E93"),sQuery(id+"F22.wireOp",EDGE,"E94"),sQuery(id+"F22.wireOp",EDGE,"E97"),sQuery(id+"F22.wireOp",EDGE,"E98.filletArc")])]});
            var Q2;
            Q2=makeQuery(id+"F15.opExtrude","SWEPT_BODY",BODY,{"disambiguationData":[OSD([sQuery(id+"F14.wireOp",EDGE,"E31.bottom"),sQuery(id+"F14.wireOp",EDGE,"E31.top"),sQuery(id+"F14.wireOp",EDGE,"E31.left"),sQuery(id+"F14.wireOp",EDGE,"E31.right"),sQuery(id+"F14.wireOp",EDGE,"E34.0"),sQuery(id+"F14.wireOp",EDGE,"E34.1")])]});
            var Q3;
            Q3=makeQuery(id+"F26.opRevolve","SWEPT_BODY",BODY,{"disambiguationData":[OSD([sQuery(id+"F25.wireOp",EDGE,"E100"),sQuery(id+"F25.wireOp",EDGE,"E101"),sQuery(id+"F25.wireOp",EDGE,"E102"),sQuery(id+"F25.wireOp",EDGE,"E103"),sQuery(id+"F25.wireOp",EDGE,"E105"),sQuery(id+"F25.wireOp",EDGE,"E106"),sQuery(id+"F25.wireOp",EDGE,"E107.filletArc")])]});
            var Q4;
            Q4=makeQuery(id+"F27.opPattern","COPY",BODY,{"derivedFrom":makeQuery(id+"F23.opRevolve","SWEPT_BODY",BODY,{"disambiguationData":[OSD([sQuery(id+"F22.wireOp",EDGE,"E62"),sQuery(id+"F22.wireOp",EDGE,"E63"),sQuery(id+"F22.wireOp",EDGE,"E64"),sQuery(id+"F22.wireOp",EDGE,"E74"),sQuery(id+"F22.wireOp",EDGE,"E75"),sQuery(id+"F22.wireOp",EDGE,"E76"),sQuery(id+"F22.wireOp",EDGE,"E77"),sQuery(id+"F22.wireOp",EDGE,"E78"),sQuery(id+"F22.wireOp",EDGE,"E79"),sQuery(id+"F22.wireOp",EDGE,"E80"),sQuery(id+"F22.wireOp",EDGE,"E81"),sQuery(id+"F22.wireOp",EDGE,"E82"),sQuery(id+"F22.wireOp",EDGE,"E83"),sQuery(id+"F22.wireOp",EDGE,"E84"),sQuery(id+"F22.wireOp",EDGE,"E85"),sQuery(id+"F22.wireOp",EDGE,"E86"),sQuery(id+"F22.wireOp",EDGE,"E87"),sQuery(id+"F22.wireOp",EDGE,"E88"),sQuery(id+"F22.wireOp",EDGE,"E89"),sQuery(id+"F22.wireOp",EDGE,"E90"),sQuery(id+"F22.wireOp",EDGE,"E91"),sQuery(id+"F22.wireOp",EDGE,"E92"),sQuery(id+"F22.wireOp",EDGE,"E93"),sQuery(id+"F22.wireOp",EDGE,"E94"),sQuery(id+"F22.wireOp",EDGE,"E97"),sQuery(id+"F22.wireOp",EDGE,"E98.filletArc")])]}),"instanceName":"1"});
            var Q5;
            Q5=makeQuery(id+"F27.opPattern","COPY",BODY,{"derivedFrom":makeQuery(id+"F21.opRevolve","SWEPT_BODY",BODY,{"disambiguationData":[OSD([sQuery(id+"F17.wireOp",EDGE,"E46"),sQuery(id+"F17.wireOp",EDGE,"E47"),sQuery(id+"F17.wireOp",EDGE,"E48"),sQuery(id+"F17.wireOp",EDGE,"E49"),sQuery(id+"F17.wireOp",EDGE,"E51"),sQuery(id+"F17.wireOp",EDGE,"E52.trimOffspring"),sQuery(id+"F17.wireOp",EDGE,"E53.1.0.0"),sQuery(id+"F17.wireOp",EDGE,"E53.2.0.0"),sQuery(id+"F17.wireOp",EDGE,"E54.0.3.0"),sQuery(id+"F17.wireOp",EDGE,"E54.0.4.0"),sQuery(id+"F17.wireOp",EDGE,"E54.0.5.0"),sQuery(id+"F17.wireOp",EDGE,"E54.0.6.0"),sQuery(id+"F17.wireOp",EDGE,"E54.0.7.0"),sQuery(id+"F17.wireOp",EDGE,"E54.0.8.0"),sQuery(id+"F17.wireOp",EDGE,"E54.0.9.0")])]}),"instanceName":"1"});
            var Q6;
            Q6=makeQuery(id+"F27.opPattern","COPY",BODY,{"derivedFrom":makeQuery(id+"F26.opRevolve","SWEPT_BODY",BODY,{"disambiguationData":[OSD([sQuery(id+"F25.wireOp",EDGE,"E100"),sQuery(id+"F25.wireOp",EDGE,"E101"),sQuery(id+"F25.wireOp",EDGE,"E102"),sQuery(id+"F25.wireOp",EDGE,"E103"),sQuery(id+"F25.wireOp",EDGE,"E105"),sQuery(id+"F25.wireOp",EDGE,"E106"),sQuery(id+"F25.wireOp",EDGE,"E107.filletArc")])]}),"instanceName":"1"});
            var Q7;
            Q7=makeQuery(id+"F27.opPattern","COPY",BODY,{"derivedFrom":makeQuery(id+"F15.opExtrude","SWEPT_BODY",BODY,{"disambiguationData":[OSD([sQuery(id+"F14.wireOp",EDGE,"E31.bottom"),sQuery(id+"F14.wireOp",EDGE,"E31.top"),sQuery(id+"F14.wireOp",EDGE,"E31.left"),sQuery(id+"F14.wireOp",EDGE,"E31.right"),sQuery(id+"F14.wireOp",EDGE,"E34.0"),sQuery(id+"F14.wireOp",EDGE,"E34.1")])]}),"instanceName":"1"});
            var Q8;
            Q8=qCreatedBy(makeId("Front.planeOp"),FACE);
            mirror(context, id + "F28", {"entities" : qUnion([Q0, Q1, Q2, Q3, Q4, Q5, Q6, Q7]), "mirrorPlane" : qUnion([Q8])});
        }
    });
